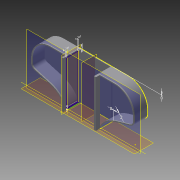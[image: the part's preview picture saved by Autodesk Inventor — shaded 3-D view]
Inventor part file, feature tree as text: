
AUTODESK INVENTOR PART (.ipt)
format: ipt  version: 2015 (Build 190159000, 159)  size: 355,840 bytes
history: native  units: mm
features: extrude x14, sketch x14, projected_geometry x9, mirror x5, plane x2
ambient origin geometry x8: Origin, YZ Plane, XZ Plane, XY Plane, X Axis, Y Axis, Z Axis, Center Point
bodies: Solid1 (feature_tree)
feature tree (44):
  extrude  "Extrusion1"  Depth=2.0mm
  sketch  "Sketch2"  dims[d2=64.0mm d3=2.0mm]
  extrude  "Extrusion3"  Depth=2.0mm
  sketch  "Sketch6"  dims[d6=2.0mm d7=2.0mm]
  extrude  "Extrusion4"  Depth=2.0mm
  extrude  "Extrusion5"  Depth=2.0mm
  plane  "Work Plane1"
  mirror  "Mirror1"
  mirror  "Mirror2"
  extrude  "Extrusion6"  Depth=2.0mm
  extrude  "Extrusion7"  Depth=96.5mm TaperAngle=0.0deg
  mirror  "Mirror3"
  sketch  "Sketch10"  dims[d18=40.0mm d20=50.0mm]
  sketch  "Sketch11"  dims[d21=10.0mm d22=2.0mm d23=0.0mm]
  sketch  "Sketch12"  dims[d24=0.0mm d25=0.0mm]
  extrude  "Extrusion10"  Depth=50.0mm
  extrude  "Extrusion11"  Depth=2.0mm TaperAngle=0.0deg
  mirror  "Mirror5"
  mirror  "Mirror6"
  extrude  "Extrusion12"  TaperAngle=0.0deg  [1 undecoded]
  extrude  "Extrusion13"  Depth=2.0mm TaperAngle=0.0deg
  extrude  "Extrusion14"  Depth=2.0mm TaperAngle=0.0deg
  extrude  "Extrusion15"  Depth=2.0mm
  sketch  "Sketch17"  dims[d38=4.0mm d43=2.0mm d44=0.0mm d45=2.0mm d46=0.0mm d47=2.0mm d48=0.0mm d49=2.0mm d50=2.0mm d51=2.0mm d52=4.0mm d53=2.0mm d54=0.0mm d55=2.0mm d56=0.0mm d57=2.0mm d58=0.0mm d59=2.0mm d60=2.0mm d61=2.0mm d62=2.0mm d63=2.0mm d64=0.0mm d65=2.0mm d66=0.0mm]
  extrude  "Extrusion16"  Depth=2.0mm
  extrude  "Extrusion17"  Depth=2.0mm TaperAngle=0.0deg
  sketch  "Sketch1"  dims[d0=24.0mm d1=2.0mm]
  projected_geometry  "Projected Loop1"
  sketch  "Sketch5"  dims[d4=24.0mm d5=2.0mm]
  projected_geometry  "Projected Loop2"
  projected_geometry  "Projected Loop3"
  sketch  "Sketch8"  dims[d8=2.0mm d9=2.0mm]
  projected_geometry  "Projected Loop4"
  sketch  "Sketch9"  dims[d10=2.0mm d11=96.5mm d12=0.0mm]
  plane  "Work Plane2"
  projected_geometry  "Projected Loop6"
  sketch  "Sketch13"  dims[d26=2.0mm d27=2.0mm d28=0.0mm]
  projected_geometry  "Projected Loop7"
  projected_geometry  "Projected Loop8"
  sketch  "Sketch14"  dims[d29=2.0mm d30=0.0mm d31=2.0mm d32=0.0mm]
  projected_geometry  "Projected Loop9"
  sketch  "Sketch15"  dims[d33=2.0mm d34=0.0mm d35=2.0mm]
  sketch  "Sketch16"  dims[d36=2.0mm d37=2.0mm]
  projected_geometry  "Projected Loop10"
note: 1 required parameter value undecoded (feature->parameter linkage not recoverable at this tier; creation-order binding heuristic only, values carry confidence <= 0.55)
